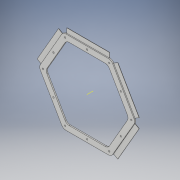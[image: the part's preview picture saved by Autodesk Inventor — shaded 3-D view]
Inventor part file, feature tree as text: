
AUTODESK INVENTOR PART (.ipt)
format: ipt  version: 2019 (Build 230136000, 136)  size: 474,112 bytes
history: native  units: mm
features: sketch x5, projected_geometry x5, extrude x4, fillet x2, other x1, pattern_circular x1, hole x1
ambient origin geometry x8: Origin, YZ Plane, XZ Plane, XY Plane, X Axis, Y Axis, Z Axis, Center Point
bodies: Solid1 (feature_tree)
feature tree (19):
  extrude  "Extrusion1"  Depth=2.0mm TaperAngle=0.0deg
  extrude  "Extrusion6"  Depth=10.0mm
  fillet  "Fillet2"  Radius=10.0mm
  fillet  "Fillet3"  Radius=12.0mm
  extrude  "Extrusion7"  Depth=0.5mm TaperAngle=0.0deg
  other  "Work Axis1"
  pattern_circular  "Circular Pattern1"  Count=6 Angle=360.0deg
  hole  "Hole1"  [1 undecoded]
  extrude  "Extrusion8"  [1 undecoded]
  sketch  "Sketch1"  dims[d0=175.0mm d1=2.0mm d2=0.0mm]
  sketch  "Sketch7"  dims[d20=7.0mm d21=0.0mm d24=10.0mm d25=10.0mm d26=12.0mm]
  projected_geometry  "Projected Loop7"
  sketch  "Sketch8"  dims[d27=10.0mm d28=0.5mm d29=0.0mm d30=60.0mm d31=360.0deg]
  projected_geometry  "Projected Loop8"
  sketch  "Sketch9"  dims[d33=60.0mm d35=360.0deg]
  projected_geometry  "Projected Loop9"
  sketch  "Sketch10"  dims[d37=3.0mm d38=6.0mm d39=10.0mm d40=2.0mm d41=90.0deg d42=26.75mm d43=0.0mm d44=10.0mm d45=0.0mm]
  projected_geometry  "Projected Loop10"
  projected_geometry  "Projected Loop11"
note: 2 required parameter values undecoded (feature->parameter linkage not recoverable at this tier; creation-order binding heuristic only, values carry confidence <= 0.55)
